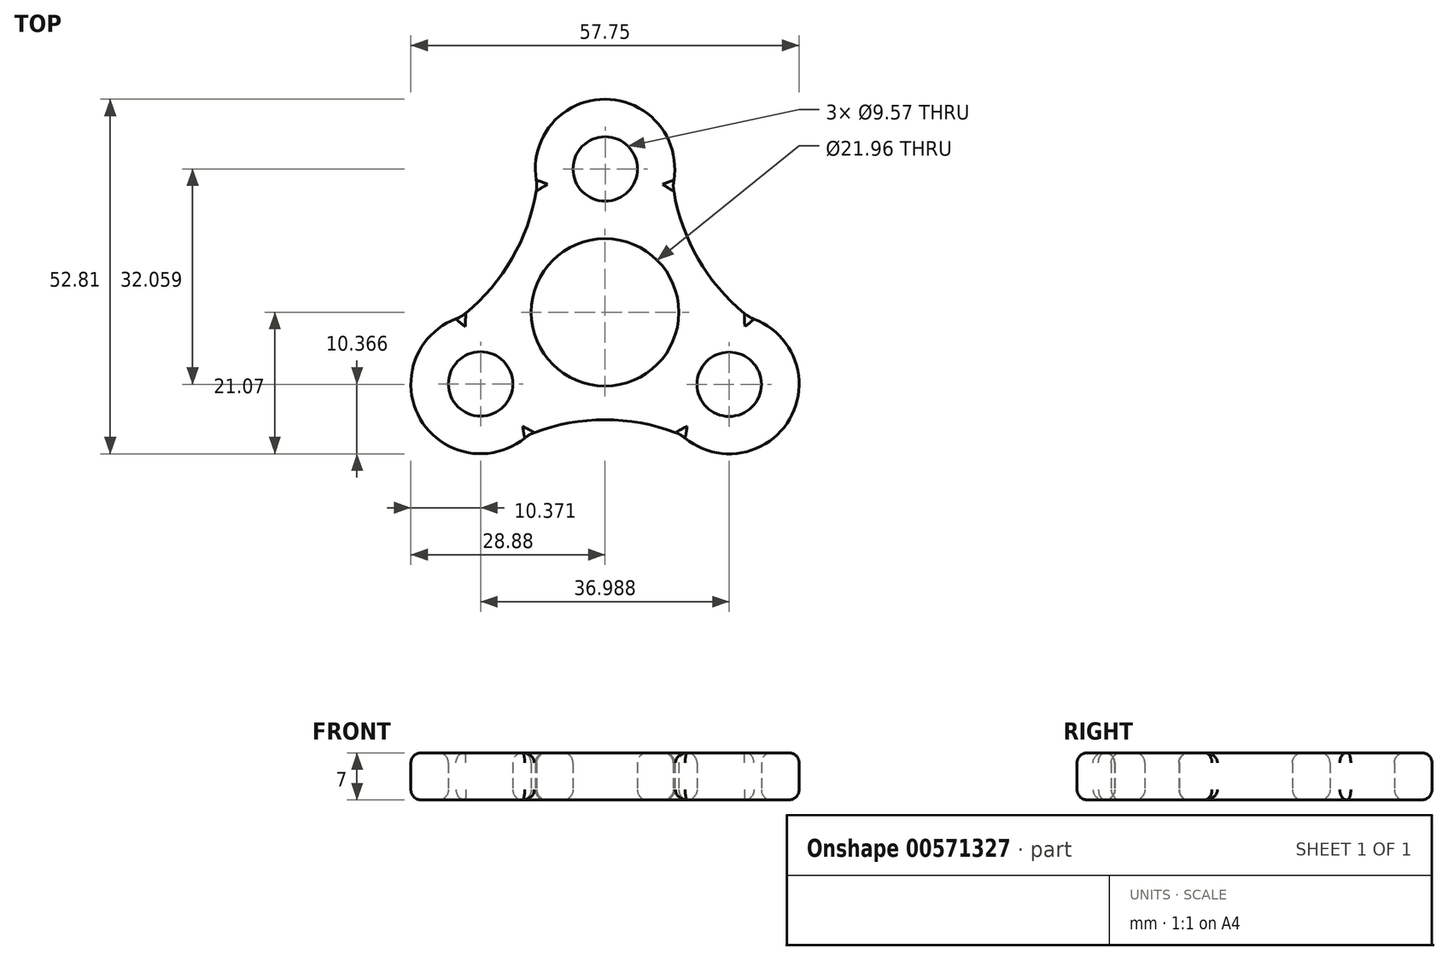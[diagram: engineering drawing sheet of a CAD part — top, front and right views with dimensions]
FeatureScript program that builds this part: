
annotation { "Feature Type Name" : "Feature", "Feature Type Description" : "" }
export const myFeature = defineFeature(function(context is Context, id is Id, definition is map)
    precondition{}
    {
        {
            var Q0;
            Q0=qCreatedBy(makeId("Top.planeOp"),FACE);
            var sketch = newSketch(context, id + "F0", { "sketchPlane" : qUnion([Q0])});
            skCircle(sketch, "E0", {"center": v(0, 0) * mm, "radius": 10.98 * mm});
            skArc(sketch, "E1", {"start": v(11.37, -18.23) * mm, "mid": v(27.48, -15.9) * mm, "end": v(21.49, -0.76) * mm});
            skArc(sketch, "E2.1.0", {"start": v(-0.03, 10.98) * mm, "mid": v(0.02, 10.98) * mm, "end": v(0.06, 10.98) * mm});
            skPoint(sketch, "E2.center", {"position": v(0.01, 0) * mm});
            skArc(sketch, "E3.1.0", {"start": v(10.1, 18.96) * mm, "mid": v(10.1, 18.93) * mm, "end": v(10.11, 18.9) * mm});
            skLineSegment(sketch, "E3.2.0", {"start": v(-21.47, -0.73) * mm, "end": v(-21.47, -0.73) * mm});
            skArc(sketch, "E4", {"start": v(10.1, 18.96) * mm, "mid": v(13.85, 7.98) * mm, "end": v(21.49, -0.76) * mm});
            skArc(sketch, "E5.trimOffspring", {"start": v(-9.33, -5.8) * mm, "mid": v(-9.5, -5.48) * mm, "end": v(-9.69, -5.17) * mm});
            skArc(sketch, "E6.1.0", {"start": v(-21.47, -0.73) * mm, "mid": v(-13.84, 8) * mm, "end": v(-10.09, 18.99) * mm});
            skArc(sketch, "E6.1.1", {"start": v(10.1, 18.96) * mm, "mid": v(0.02, 31.74) * mm, "end": v(-10.09, 18.99) * mm});
            skArc(sketch, "E6.2.0", {"start": v(11.37, -18.23) * mm, "mid": v(-0.01, -15.99) * mm, "end": v(-11.4, -18.23) * mm});
            skArc(sketch, "E6.2.1", {"start": v(-21.47, -0.73) * mm, "mid": v(-27.5, -15.85) * mm, "end": v(-11.4, -18.23) * mm});
            skCircle(sketch, "E7", {"center": v(0.03, 21.35) * mm, "radius": 4.79 * mm});
            skCircle(sketch, "E8.1.0", {"center": v(-18.5, -10.65) * mm, "radius": 4.79 * mm});
            skCircle(sketch, "E8.2.0", {"center": v(18.48, -10.7) * mm, "radius": 4.79 * mm});
            skSolve(sketch);
        }
        {
            var Q0;
            Q0 = qSketchRegion(id + "F0", true);
            extrude(context, id + "F1", {"entities" : qUnion([Q0]), "depth" : 7 * mm, "offsetDistance" : 25 * mm});
        }
        {
            var Q0;
            Q0=makeQuery(id+"F1.opExtrude","CAP_FACE",FACE,{"disambiguationData":[OSD([sQuery(id+"F0.wireOp",EDGE,"E0"),sQuery(id+"F0.wireOp",EDGE,"TRz7FE7b-hP9j-DVcV-AFGB-AedisKRbFC56"),sQuery(id+"F0.wireOp",EDGE,"718798ef-7430-437e-bcb6-37eee1c87575.1.0"),sQuery(id+"F0.wireOp",EDGE,"718798ef-7430-437e-bcb6-37eee1c87575.2.0"),sQuery(id+"F0.wireOp",EDGE,"E1"),sQuery(id+"F0.wireOp",EDGE,"E4"),sQuery(id+"F0.wireOp",EDGE,"E6.1.0"),sQuery(id+"F0.wireOp",EDGE,"E6.1.1"),sQuery(id+"F0.wireOp",EDGE,"E6.2.0"),sQuery(id+"F0.wireOp",EDGE,"E6.2.1")])],"isStart":false});
            var Q1;
            Q1=makeQuery(id+"F1.opExtrude","CAP_FACE",FACE,{"disambiguationData":[OSD([sQuery(id+"F0.wireOp",EDGE,"E0"),sQuery(id+"F0.wireOp",EDGE,"TRz7FE7b-hP9j-DVcV-AFGB-AedisKRbFC56"),sQuery(id+"F0.wireOp",EDGE,"718798ef-7430-437e-bcb6-37eee1c87575.1.0"),sQuery(id+"F0.wireOp",EDGE,"718798ef-7430-437e-bcb6-37eee1c87575.2.0"),sQuery(id+"F0.wireOp",EDGE,"E1"),sQuery(id+"F0.wireOp",EDGE,"E4"),sQuery(id+"F0.wireOp",EDGE,"E6.1.0"),sQuery(id+"F0.wireOp",EDGE,"E6.1.1"),sQuery(id+"F0.wireOp",EDGE,"E6.2.0"),sQuery(id+"F0.wireOp",EDGE,"E6.2.1")])],"isStart":true});
            fillet(context, id + "F2", {"entities" : qUnion([Q0, Q1]), "radius" : 1.5 * mm, "tangentPropagation" : true, "allowEdgeOverflow" : false});
        }
        {
            var Q0;
            Q0=makeQuery(id+"F1.opExtrude","SWEPT_EDGE",EDGE,{"disambiguationData":[OSD([sQuery(id+"F0.wireOp",EDGE,"E6.1.0"),sQuery(id+"F0.wireOp",EDGE,"E6.2.1")])]});
            var Q1;
            Q1=makeQuery(id+"F1.opExtrude","SWEPT_EDGE",EDGE,{"disambiguationData":[OSD([sQuery(id+"F0.wireOp",EDGE,"E6.1.0"),sQuery(id+"F0.wireOp",EDGE,"E6.1.1")])]});
            var Q2;
            Q2=makeQuery(id+"F1.opExtrude","SWEPT_EDGE",EDGE,{"disambiguationData":[OSD([sQuery(id+"F0.wireOp",EDGE,"E4"),sQuery(id+"F0.wireOp",EDGE,"E6.1.1")])]});
            var Q3;
            Q3=makeQuery(id+"F1.opExtrude","SWEPT_EDGE",EDGE,{"disambiguationData":[OSD([sQuery(id+"F0.wireOp",EDGE,"E1"),sQuery(id+"F0.wireOp",EDGE,"E4")])]});
            var Q4;
            Q4=makeQuery(id+"F1.opExtrude","SWEPT_EDGE",EDGE,{"disambiguationData":[OSD([sQuery(id+"F0.wireOp",EDGE,"E6.2.0"),sQuery(id+"F0.wireOp",EDGE,"E6.2.1")])]});
            var Q5;
            Q5=makeQuery(id+"F1.opExtrude","SWEPT_EDGE",EDGE,{"disambiguationData":[OSD([sQuery(id+"F0.wireOp",EDGE,"E1"),sQuery(id+"F0.wireOp",EDGE,"E6.2.0")])]});
            fillet(context, id + "F3", {"entities" : qUnion([Q0, Q1, Q2, Q3, Q4, Q5]), "radius" : 5 * mm, "tangentPropagation" : true, "allowEdgeOverflow" : false});
        }
    });
